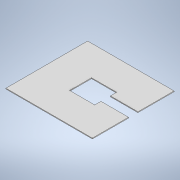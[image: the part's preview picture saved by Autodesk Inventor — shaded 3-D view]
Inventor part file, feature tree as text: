
AUTODESK INVENTOR PART (.ipt)
format: ipt  version: 2022.3 (Build 263350000, 350)  size: 104,960 bytes
history: native  units: in
note: dims shown in document units (in); Inventor stores cm internally (conversion verified against a paired STEP export)
features: extrude x1, sketch x1
ambient origin geometry x8: Origin, YZ Plane, XZ Plane, XY Plane, X Axis, Y Axis, Z Axis, Center Point
bodies: Solid1 (feature_tree)
feature tree (2):
  extrude  "Extrusion1"  Depth=4.0945in
  sketch  "Sketch1"  dims[d6=4.3307in d7=4.0945in d8=0.4724in d9=1.811in d10=1.2598in d11=1.1024in d12=1.378in d13=0.0394in d14=0.0in]
